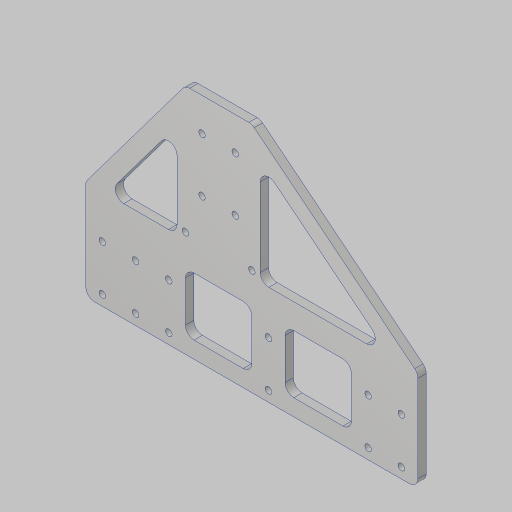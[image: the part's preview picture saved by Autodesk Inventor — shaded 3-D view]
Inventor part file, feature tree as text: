
AUTODESK INVENTOR PART (.ipt)
format: ipt  version: 2023.5 (Build 275446000, 446)  size: 238,080 bytes
history: native  units: in
note: dims shown in document units (in); Inventor stores cm internally (conversion verified against a paired STEP export)
features: sketch x2, extrude x2, fillet x2, hole x1, projected_geometry x1
ambient origin geometry x8: Origin, YZ Plane, XZ Plane, XY Plane, X Axis, Y Axis, Z Axis, Center Point
bodies: Solid1 (feature_tree)
feature tree (8):
  sketch  "Sketch1"  dims[d0=2.0in d1=8.0in]
  extrude  "Extrusion1"  Depth=8.0in
  hole  "Hole1"  [1 undecoded]
  fillet  "Fillet1"  Radius=5.0in
  extrude  "Extrusion2"  Depth=0.5in
  fillet  "Fillet2"  Radius=0.5in
  sketch  "Sketch2"  dims[d2=10.0in d3=3.0in d4=5.0in d5=0.5in d6=0.5in d7=0.375in d8=0.125in d9=0.375in d10=3.937in d12=1.0in d13=0.3937in d15=1.0in d17=1.0in d18=1.375in d19=1.0in d20=0.5in d21=0.375in d22=0.375in d23=0.25in d24=0.0in d25=0.201in d26=0.75in d27=0.385in d28=0.25in d29=0.5635in d30=1.0in d31=0.8108in d32=4.375in d33=1.625in d34=0.26in d35=0.5in d36=0.5in d37=0.375in d38=2.0in d39=1.375in d40=0.25in d41=0.25in d44=0.5in d45=0.75in d46=1.0in d47=0.0in d48=0.26in d49=0.5in d50=0.5in d51=0.5in d52=0.5in d53=0.5in d54=0.5in]
  projected_geometry  "Project Cut Edges1"
note: 1 required parameter value undecoded (feature->parameter linkage not recoverable at this tier; creation-order binding heuristic only, values carry confidence <= 0.55)
